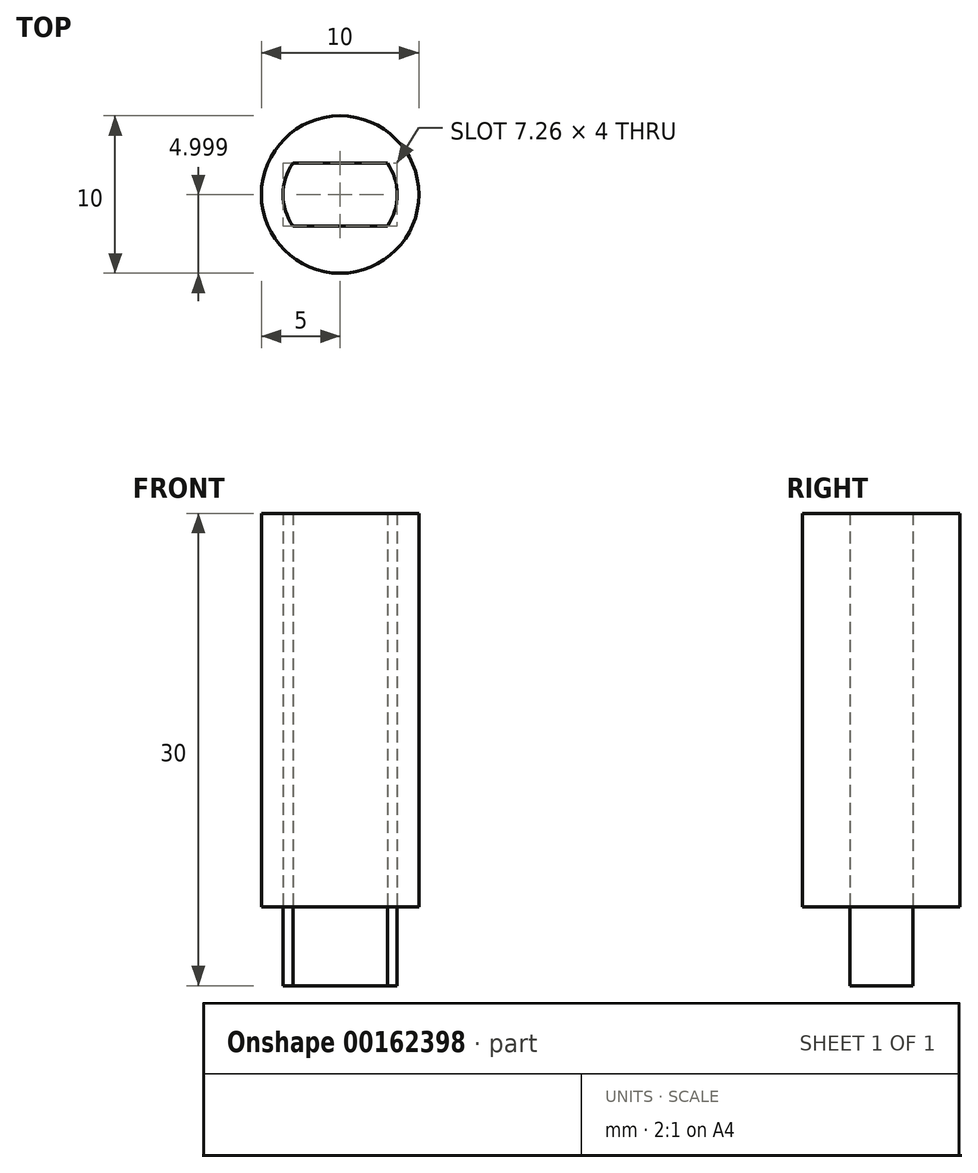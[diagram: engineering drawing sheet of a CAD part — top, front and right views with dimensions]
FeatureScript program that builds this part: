
annotation { "Feature Type Name" : "Feature", "Feature Type Description" : "" }
export const myFeature = defineFeature(function(context is Context, id is Id, definition is map)
    precondition{}
    {
        {
            var Q0;
            Q0=qCreatedBy(makeId("Top.planeOp"),FACE);
            var sketch = newSketch(context, id + "F0", { "sketchPlane" : qUnion([Q0])});
            skLineSegment(sketch, "E0.bottom", {"start": v(-47.59, -29.68) * mm, "end": v(-37.59, -29.68) * mm});
            skLineSegment(sketch, "E0.top", {"start": v(-47.59, -39.68) * mm, "end": v(-37.59, -39.68) * mm});
            skLineSegment(sketch, "E0.left", {"start": v(-47.59, -29.68) * mm, "end": v(-47.59, -39.68) * mm});
            skLineSegment(sketch, "E0.right", {"start": v(-37.59, -29.68) * mm, "end": v(-37.59, -39.68) * mm});
            skLineSegment(sketch, "E1.bottom", {"start": v(-45.59, -32.68) * mm, "end": v(-39.59, -32.68) * mm});
            skLineSegment(sketch, "E1.top", {"start": v(-45.59, -36.68) * mm, "end": v(-39.59, -36.68) * mm});
            skLineSegment(sketch, "E1.left", {"start": v(-45.59, -32.68) * mm, "end": v(-45.59, -36.68) * mm});
            skLineSegment(sketch, "E1.right", {"start": v(-39.59, -32.68) * mm, "end": v(-39.59, -36.68) * mm});
            skArc(sketch, "E2", {"start": v(-39.59, -36.68) * mm, "mid": v(-38.96, -34.68) * mm, "end": v(-39.59, -32.68) * mm});
            skArc(sketch, "E3", {"start": v(-45.59, -32.68) * mm, "mid": v(-46.22, -34.68) * mm, "end": v(-45.59, -36.68) * mm});
            skSolve(sketch);
        }
        {
            var Q0;
            Q0 = qSketchRegion(id + "F0", true);
            extrude(context, id + "F1", {"entities" : qUnion([Q0]), "depth" : 25 * mm});
        }
        {
            var Q0;
            Q0=makeQuery(id+"F1.opExtrude","SWEPT_EDGE",EDGE,{"disambiguationData":[OSD([sQuery(id+"F0.wireOp",EDGE,"E0.top"),sQuery(id+"F0.wireOp",EDGE,"E0.right")])]});
            var Q1;
            Q1=makeQuery(id+"F1.opExtrude","SWEPT_EDGE",EDGE,{"disambiguationData":[OSD([sQuery(id+"F0.wireOp",EDGE,"E0.bottom"),sQuery(id+"F0.wireOp",EDGE,"E0.right")])]});
            var Q2;
            Q2=makeQuery(id+"F1.opExtrude","SWEPT_EDGE",EDGE,{"disambiguationData":[OSD([sQuery(id+"F0.wireOp",EDGE,"E0.top"),sQuery(id+"F0.wireOp",EDGE,"E0.left")])]});
            var Q3;
            Q3=makeQuery(id+"F1.opExtrude","SWEPT_EDGE",EDGE,{"disambiguationData":[OSD([sQuery(id+"F0.wireOp",EDGE,"E0.bottom"),sQuery(id+"F0.wireOp",EDGE,"E0.left")])]});
            fillet(context, id + "F2", {"entities" : qUnion([Q0, Q1, Q2, Q3]), "radius" : 5 * mm, "tangentPropagation" : true, "allowEdgeOverflow" : false});
        }
        {
            var Q0;
            Q0=makeQuery(id+"F0.imprint","IMPRINT",FACE,{"disambiguationData":[TD([[makeQuery(id+"F0.imprint","IMPRINT",EDGE,{"derivedFrom":sQuery(id+"F0.wireOp",EDGE,"E1.bottom")}),-1.0]])]});
            var Q1;
            Q1=makeQuery(id+"F0.imprint","IMPRINT",FACE,{"disambiguationData":[TD([[makeQuery(id+"F0.imprint","IMPRINT",EDGE,{"derivedFrom":sQuery(id+"F0.wireOp",EDGE,"E1.left")}),-1.0]])]});
            var Q2;
            Q2=makeQuery(id+"F0.imprint","IMPRINT",FACE,{"disambiguationData":[TD([[makeQuery(id+"F0.imprint","IMPRINT",EDGE,{"derivedFrom":sQuery(id+"F0.wireOp",EDGE,"E1.right")}),1.0]])]});
            extrude(context, id + "F3", {"entities" : qUnion([Q0, Q1, Q2]), "operationType" : NewBodyOperationType.ADD, "oppositeDirection" : true, "depth" : 5 * mm});
        }
    });
